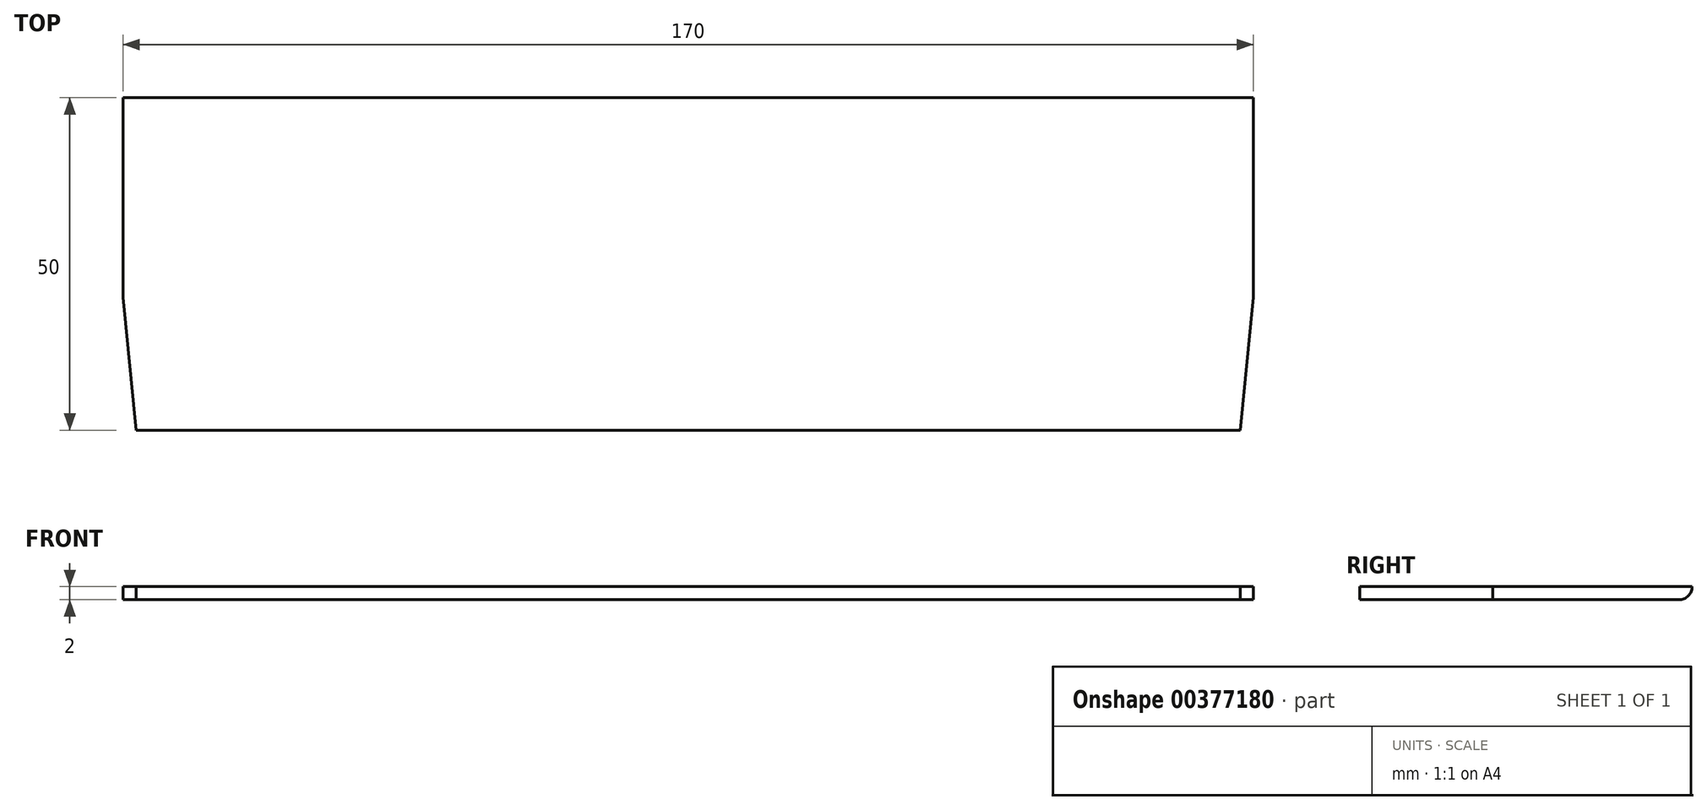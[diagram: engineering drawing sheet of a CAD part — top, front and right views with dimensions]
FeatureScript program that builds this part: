
annotation { "Feature Type Name" : "Feature", "Feature Type Description" : "" }
export const myFeature = defineFeature(function(context is Context, id is Id, definition is map)
    precondition{}
    {
        {
            var Q0;
            Q0=qCreatedBy(makeId("Top.planeOp"),FACE);
            var sketch = newSketch(context, id + "F0", { "sketchPlane" : qUnion([Q0])});
            skLineSegment(sketch, "E0.bottom", {"start": v(-85.43, 0.68) * mm, "end": v(84.57, 0.68) * mm});
            skLineSegment(sketch, "E0.top", {"start": v(-83.43, -47.32) * mm, "end": v(82.57, -47.32) * mm});
            skLineSegment(sketch, "E0.left", {"start": v(-85.43, 0.68) * mm, "end": v(-85.43, -27.32) * mm});
            skLineSegment(sketch, "E0.right", {"start": v(84.57, 0.68) * mm, "end": v(84.57, -27.32) * mm});
            skLineSegment(sketch, "E1", {"start": v(-83.43, -47.32) * mm, "end": v(-85.43, -27.32) * mm});
            skLineSegment(sketch, "E2.MirrorCS", {"start": v(82.57, -47.32) * mm, "end": v(84.57, -27.32) * mm});
            skPoint(sketch, "E3.orphan", {"position": v(-85.43, -47.32) * mm});
            skPoint(sketch, "E4.start.orphan", {"position": v(-0.43, -47.32) * mm});
            skPoint(sketch, "E5.orphan", {"position": v(84.57, -47.32) * mm});
            skSolve(sketch);
        }
        {
            var Q0;
            Q0=makeQuery(id+"F0.imprint","IMPRINT",FACE,{"disambiguationData":[TD([[makeQuery(id+"F0.imprint","IMPRINT",EDGE,{"derivedFrom":sQuery(id+"F0.wireOp",EDGE,"E0.bottom")}),-1.0]])]});
            extrude(context, id + "F1", {"entities" : qUnion([Q0]), "depth" : 2 * mm});
        }
        {
            var Q0;
            Q0=makeQuery(id+"F1.opExtrude","SWEPT_FACE",FACE,{"disambiguationData":[OSD([sQuery(id+"F0.wireOp",EDGE,"E0.right")])]});
            var sketch = newSketch(context, id + "F2", { "sketchPlane" : qUnion([Q0])});
            skArc(sketch, "E6", {"start": v(0.68, 0) * mm, "mid": v(2.1, 0.59) * mm, "end": v(2.68, 2) * mm});
            skLineSegment(sketch, "E7", {"start": v(0.68, 2) * mm, "end": v(2.68, 2) * mm});
            skSolve(sketch);
        }
        {
            var Q0;
            Q0=makeQuery(id+"F2.imprint","IMPRINT",FACE,{"disambiguationData":[TD([[makeQuery(id+"F2.imprint","IMPRINT",EDGE,{"derivedFrom":sQuery(id+"F2.wireOp",EDGE,"E6")}),1.0]])]});
            extrude(context, id + "F3", {"entities" : qUnion([Q0]), "operationType" : NewBodyOperationType.ADD, "oppositeDirection" : true, "depth" : 170 * mm});
        }
    });
